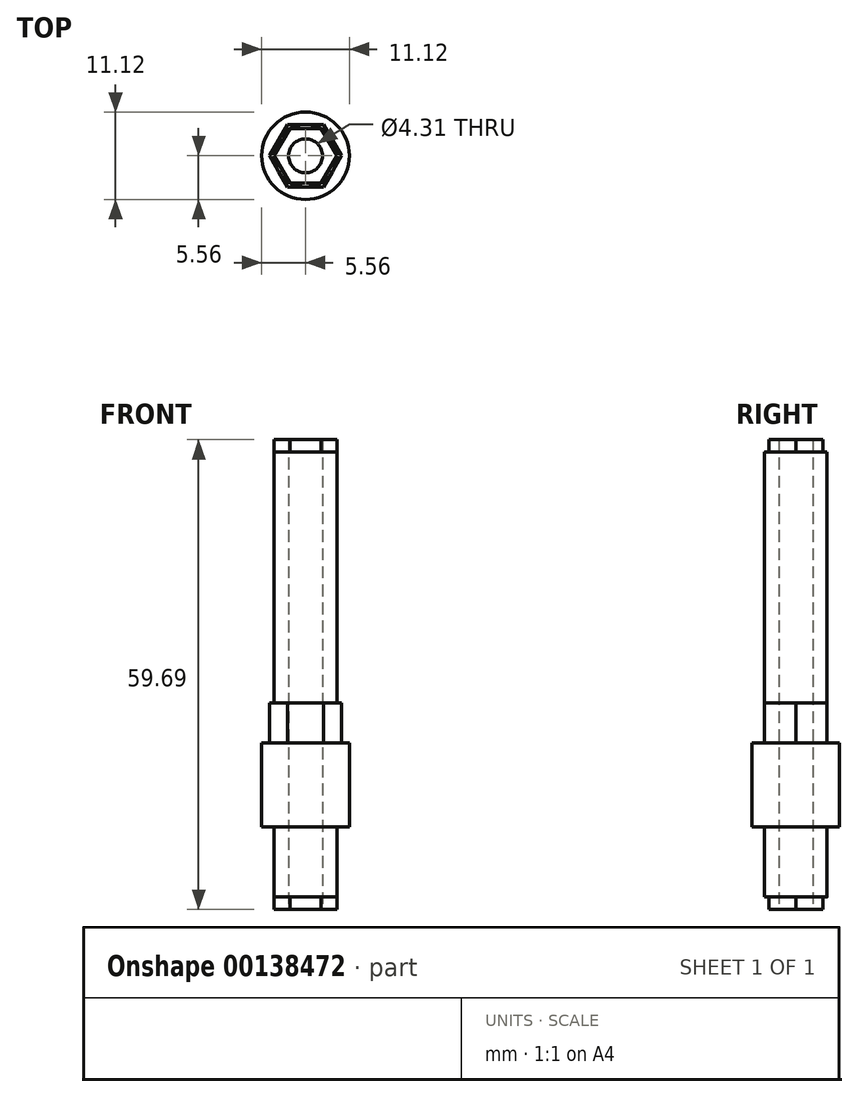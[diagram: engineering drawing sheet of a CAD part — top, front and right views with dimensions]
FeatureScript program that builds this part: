
annotation { "Feature Type Name" : "Feature", "Feature Type Description" : "" }
export const myFeature = defineFeature(function(context is Context, id is Id, definition is map)
    precondition{}
    {
        {
            var Q0;
            Q0=qCreatedBy(makeId("Top.planeOp"),FACE);
            var sketch = newSketch(context, id + "F0", { "sketchPlane" : qUnion([Q0])});
            skCircle(sketch, "E0", {"center": v(0, 0) * mm, "radius": 3.97 * mm});
            skCircle(sketch, "E1", {"center": v(0, 0) * mm, "radius": 2.15 * mm});
            skSolve(sketch);
        }
        {
            var Q0;
            Q0 = qSketchRegion(id + "F0", true);
            extrude(context, id + "F1", {"entities" : qUnion([Q0]), "depth" : 56.52 * mm});
        }
        {
            var Q0;
            Q0=makeQuery(id+"F1.opExtrude","CAP_FACE",FACE,{"disambiguationData":[OSD([sQuery(id+"F0.wireOp",EDGE,"E0"),sQuery(id+"F0.wireOp",EDGE,"E1")])],"isStart":false});
            cPlane(context, id + "F2", {"entities" : qUnion([Q0]), "cplaneType" : CPlaneType.OFFSET, "offset" : 1.59 * mm, "width" : 152.4 * mm, "height" : 152.4 * mm});
        }
        {
            var Q0;
            Q0=makeQuery(id+"F1.opExtrude","CAP_FACE",FACE,{"disambiguationData":[OSD([sQuery(id+"F0.wireOp",EDGE,"E0"),sQuery(id+"F0.wireOp",EDGE,"E1")])],"isStart":true});
            var sketch = newSketch(context, id + "F3", { "sketchPlane" : qUnion([Q0])});
            skCircle(sketch, "E2.cCircle", {"center": v(0, 0) * mm, "radius": 3.97 * mm, "construction": true});
            skLineSegment(sketch, "E2.0", {"start": v(1.98, -3.44) * mm, "end": v(-1.98, -3.44) * mm});
            skLineSegment(sketch, "E2.1", {"start": v(-1.98, -3.44) * mm, "end": v(-3.97, 0) * mm});
            skLineSegment(sketch, "E2.2", {"start": v(-3.97, 0) * mm, "end": v(-1.98, 3.44) * mm});
            skLineSegment(sketch, "E2.3", {"start": v(-1.98, 3.44) * mm, "end": v(1.98, 3.44) * mm});
            skLineSegment(sketch, "E2.4", {"start": v(1.98, 3.44) * mm, "end": v(3.97, 0) * mm});
            skLineSegment(sketch, "E2.5", {"start": v(3.97, 0) * mm, "end": v(1.98, -3.44) * mm});
            skCircle(sketch, "E3", {"center": v(0, 0) * mm, "radius": 2.15 * mm});
            skSolve(sketch);
        }
        {
            var Q0;
            Q0 = qSketchRegion(id + "F3", true);
            var Q1;
            Q1=qCreatedBy(id+"F2.planeOp",FACE);
            extrude(context, id + "F4", {"entities" : qUnion([Q0]), "operationType" : NewBodyOperationType.ADD, "depth" : 1.59 * mm, "hasSecondDirection" : true, "secondDirectionBound" : SecondDirectionBoundingType.UP_TO_SURFACE, "secondDirectionOppositeDirection" : true, "secondDirectionBoundEntityFace" : qUnion([Q1]), "secondDirectionDepth" : 25.4 * mm});
        }
        {
            var Q0;
            {var subQ0=sQuery(id+"F0.wireOp",EDGE,"E0");var subQ1=makeQuery(id+"F1.opExtrude","CAP_FACE",FACE,{"disambiguationData":[OSD([subQ0,sQuery(id+"F0.wireOp",EDGE,"E1")])],"isStart":true});Q0=makeQuery(id+"F4.boolean.opBoolean","SPLIT",FACE,{"disambiguationData":[TD([makeQuery(id+"F1.opExtrude","SWEPT_FACE",FACE,{"disambiguationData":[OSD([subQ0])]}),subQ1,makeQuery(id+"F4.opExtrude","SWEPT_FACE",FACE,{"disambiguationData":[OSD([sQuery(id+"F3.wireOp",EDGE,"E2.1")])]}),makeQuery(id+"F4.opExtrude","SWEPT_FACE",FACE,{"disambiguationData":[OSD([sQuery(id+"F3.wireOp",EDGE,"E2.2")])]}),makeQuery(id+"F4.opExtrude","SWEPT_FACE",FACE,{"disambiguationData":[OSD([sQuery(id+"F3.wireOp",EDGE,"E2.3")])]})])],"derivedFrom":subQ1});}
            cPlane(context, id + "F5", {"entities" : qUnion([Q0]), "cplaneType" : CPlaneType.OFFSET, "offset" : 8.9 * mm, "oppositeDirection" : true, "width" : 152.4 * mm, "height" : 152.4 * mm});
        }
        {
            var Q0;
            Q0=qCreatedBy(id+"F5.planeOp",FACE);
            var sketch = newSketch(context, id + "F6", { "sketchPlane" : qUnion([Q0])});
            skCircle(sketch, "E4", {"center": v(0, 0) * mm, "radius": 5.56 * mm});
            skCircle(sketch, "E5", {"center": v(0, 0) * mm, "radius": 2.15 * mm});
            skSolve(sketch);
        }
        {
            var Q0;
            Q0 = qSketchRegion(id + "F6", true);
            var Q1;
            Q1=qCreatedBy(id+"FUkhTb0ER2juddy_1.planeOp",FACE);
            extrude(context, id + "F7", {"entities" : qUnion([Q0]), "operationType" : NewBodyOperationType.ADD, "oppositeDirection" : true, "endBoundEntityFace" : qUnion([Q1]), "depth" : 10.66 * mm});
        }
        {
            var Q0;
            Q0=makeQuery(id+"F7.opExtrude","CAP_FACE",FACE,{"disambiguationData":[OSD([sQuery(id+"F6.wireOp",EDGE,"E4"),sQuery(id+"F6.wireOp",EDGE,"E5")])],"isStart":false});
            var sketch = newSketch(context, id + "F8", { "sketchPlane" : qUnion([Q0])});
            skCircle(sketch, "E6.cCircle", {"center": v(0, 0) * mm, "radius": 3.97 * mm, "construction": true});
            skLineSegment(sketch, "E6.0", {"start": v(2.3, -3.97) * mm, "end": v(-2.3, -3.97) * mm});
            skLineSegment(sketch, "E6.1", {"start": v(-2.3, -3.97) * mm, "end": v(-4.58, 0) * mm});
            skLineSegment(sketch, "E6.2", {"start": v(-4.58, 0) * mm, "end": v(-2.3, 3.97) * mm});
            skLineSegment(sketch, "E6.3", {"start": v(-2.3, 3.97) * mm, "end": v(2.3, 3.97) * mm});
            skLineSegment(sketch, "E6.4", {"start": v(2.3, 3.97) * mm, "end": v(4.58, 0) * mm});
            skLineSegment(sketch, "E6.5", {"start": v(4.58, 0) * mm, "end": v(2.3, -3.97) * mm});
            skPoint(sketch, "E6.0.midPoint", {"position": v(0, -3.97) * mm});
            skCircle(sketch, "E7", {"center": v(0, 0) * mm, "radius": 2.15 * mm});
            skSolve(sketch);
        }
        {
            var Q0;
            Q0 = qSketchRegion(id + "F8", true);
            extrude(context, id + "F9", {"entities" : qUnion([Q0]), "operationType" : NewBodyOperationType.ADD, "depth" : 5.08 * mm});
        }
    });
